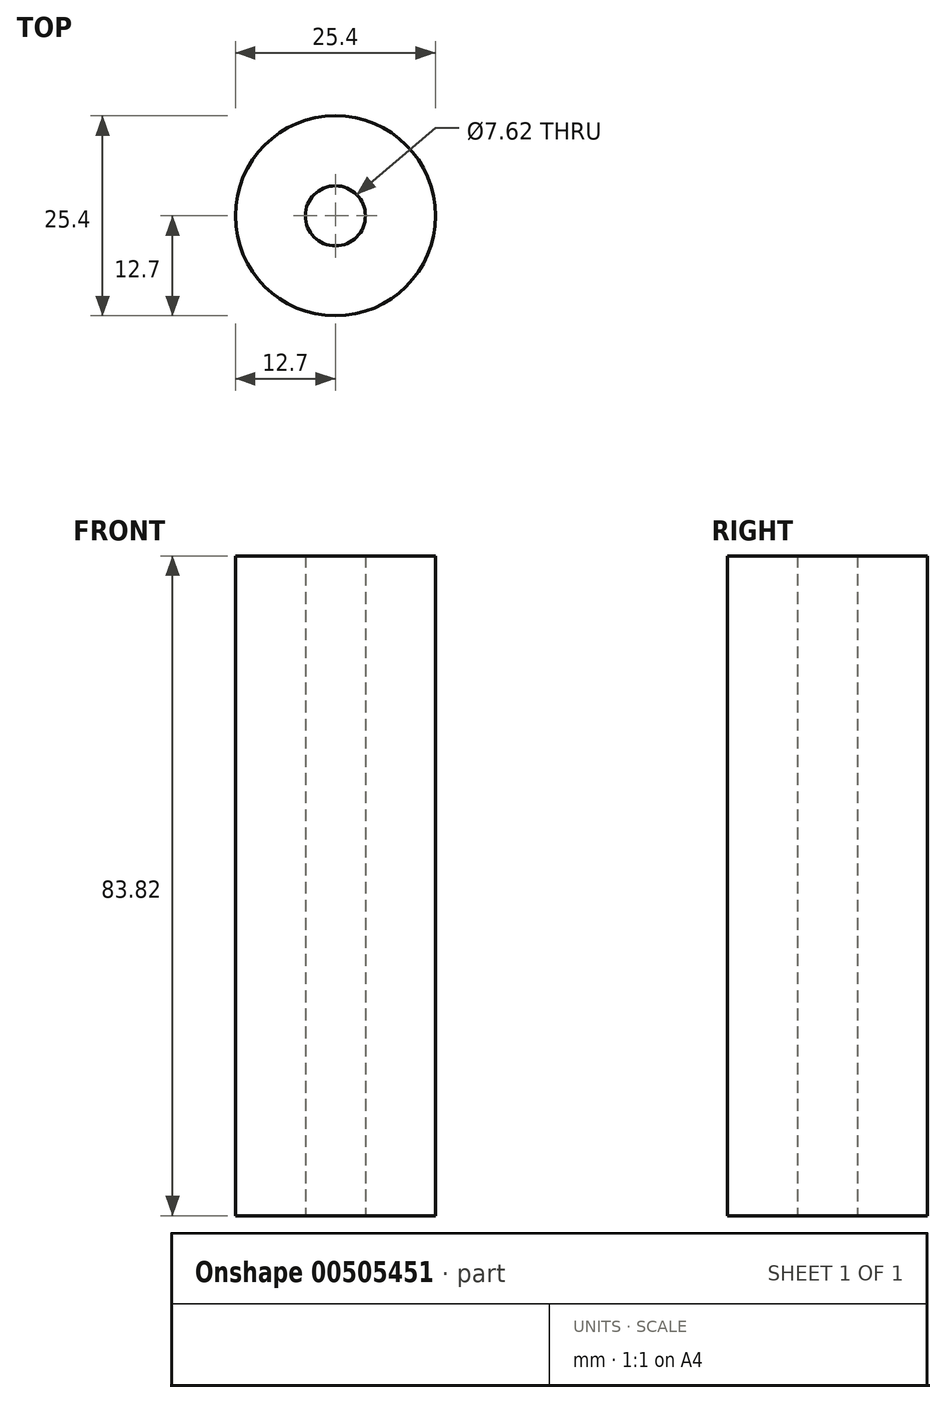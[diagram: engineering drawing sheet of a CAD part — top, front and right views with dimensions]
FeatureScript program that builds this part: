
annotation { "Feature Type Name" : "Feature", "Feature Type Description" : "" }
export const myFeature = defineFeature(function(context is Context, id is Id, definition is map)
    precondition{}
    {
        {
            var Q0;
            Q0=qCreatedBy(makeId("Top.planeOp"),FACE);
            var sketch = newSketch(context, id + "F0", { "sketchPlane" : qUnion([Q0])});
            skCircle(sketch, "E0", {"center": v(0, 0) * mm, "radius": 12.7 * mm});
            skCircle(sketch, "E1", {"center": v(0, 0) * mm, "radius": 3.81 * mm});
            skSolve(sketch);
        }
        {
            var Q0;
            Q0 = qSketchRegion(id + "F0", true);
            extrude(context, id + "F1", {"entities" : qUnion([Q0]), "depth" : 83.82 * mm});
        }
    });
